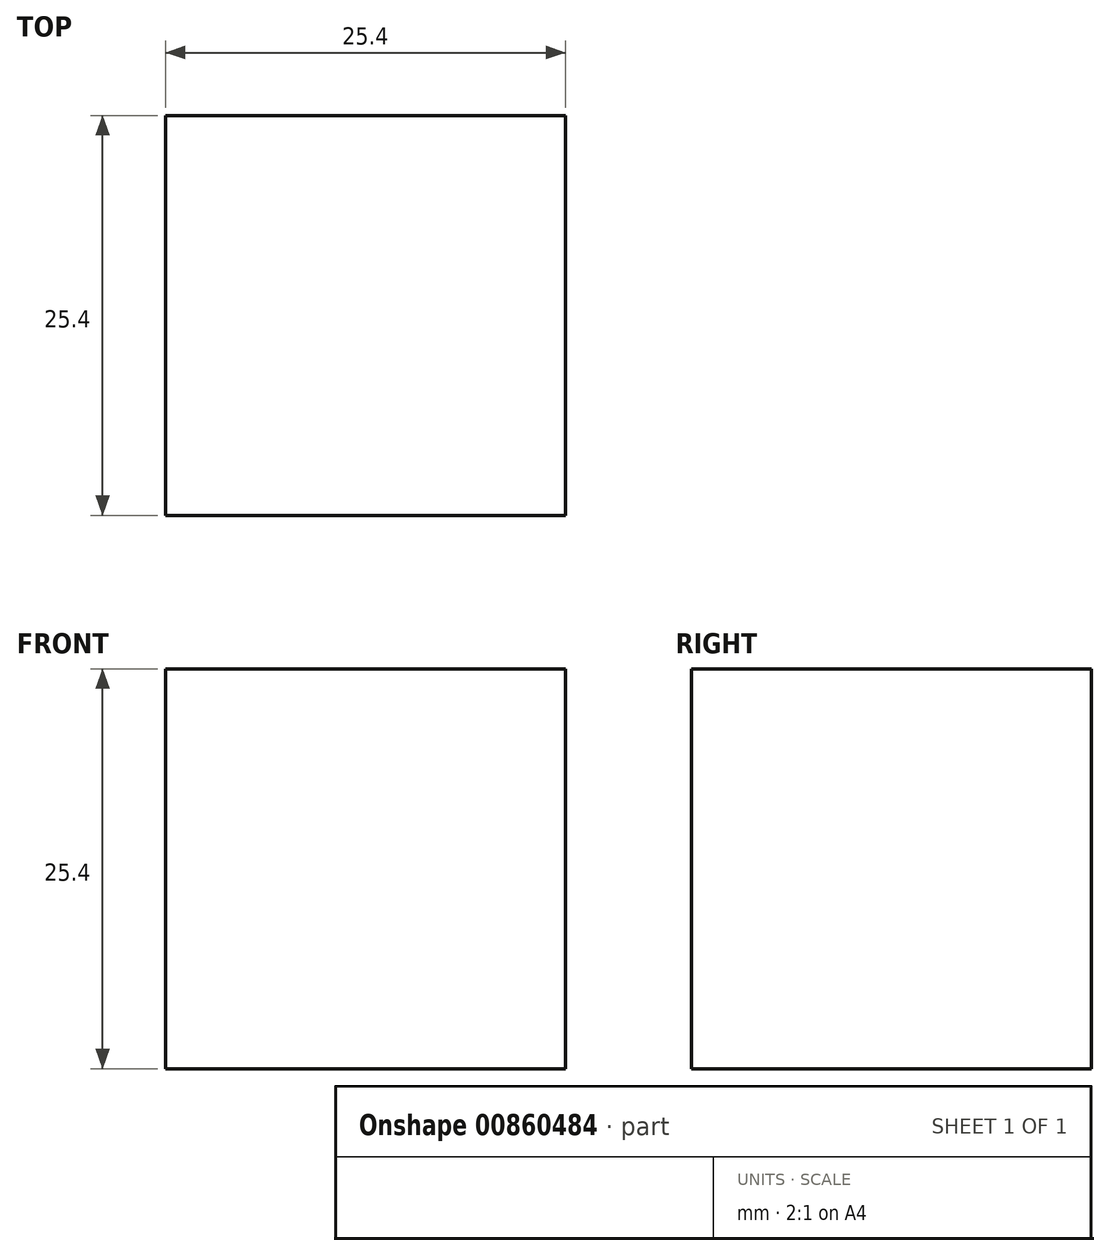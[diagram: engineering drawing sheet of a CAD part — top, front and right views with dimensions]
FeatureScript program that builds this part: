
annotation { "Feature Type Name" : "Feature", "Feature Type Description" : "" }
export const myFeature = defineFeature(function(context is Context, id is Id, definition is map)
    precondition{}
    {
        {
            var Q0;
            Q0=qCreatedBy(makeId("Top.planeOp"),FACE);
            var sketch = newSketch(context, id + "F0", { "sketchPlane" : qUnion([Q0])});
            skLineSegment(sketch, "E0.bottom", {"start": v(-12.7, 12.7) * mm, "end": v(12.7, 12.7) * mm});
            skLineSegment(sketch, "E0.top", {"start": v(-12.7, -12.7) * mm, "end": v(12.7, -12.7) * mm});
            skLineSegment(sketch, "E0.left", {"start": v(-12.7, 12.7) * mm, "end": v(-12.7, -12.7) * mm});
            skLineSegment(sketch, "E0.right", {"start": v(12.7, 12.7) * mm, "end": v(12.7, -12.7) * mm});
            skPoint(sketch, "E0.middle", {"position": v(0, 0) * mm});
            skSolve(sketch);
        }
        {
            var Q0;
            Q0=makeQuery(id+"F0.imprint","IMPRINT",FACE,{"disambiguationData":[TD([[makeQuery(id+"F0.imprint","IMPRINT",EDGE,{"derivedFrom":sQuery(id+"F0.wireOp",EDGE,"E0.bottom")}),-1.0]])]});
            extrude(context, id + "F1", {"entities" : qUnion([Q0]), "depth" : 25.4 * mm, "offsetDistance" : 25.4 * mm});
        }
    });
